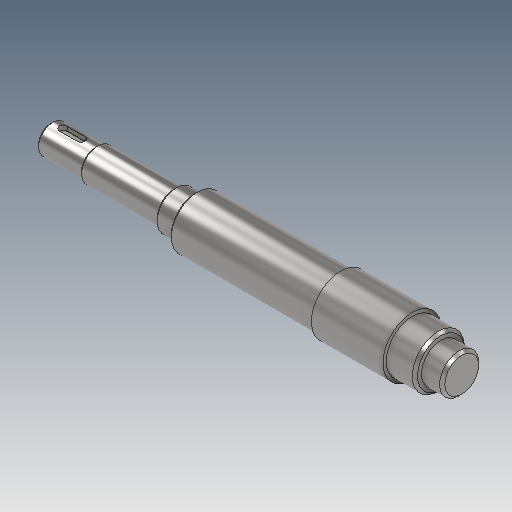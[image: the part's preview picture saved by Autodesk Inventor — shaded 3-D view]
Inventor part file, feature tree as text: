
AUTODESK INVENTOR PART (.ipt)
format: ipt  version: 2025 (Build 290162000, 162)  size: 207,360 bytes
history: native  units: mm
features: chamfer x6, other x5, revolve x1
ambient origin geometry x6: Origin, XZ Plane, XY Plane, X Axis, Y Axis, Z Axis
bodies: 实体1 (feature_tree)
feature tree (12):
  other  "{BB8FE430-83BF-418D-8DF9-9B323D3DB9B9}"
  revolve  "旋转1"  [1 undecoded]
  chamfer  "倒角1"  Distance=22.0mm
  chamfer  "倒角2"  Distance=25.0mm
  chamfer  "倒角3"  Distance=30.0mm
  chamfer  "倒角4"  Distance=40.0mm
  chamfer  "倒角5"  Distance=45.0mm
  chamfer  "倒角6"  Distance=40.0mm
  other  "键槽1"
  other  "起始平面"
  other  "主草图"
  other  "轴键槽"
note: 1 required parameter value undecoded (feature->parameter linkage not recoverable at this tier; creation-order binding heuristic only, values carry confidence <= 0.55)
